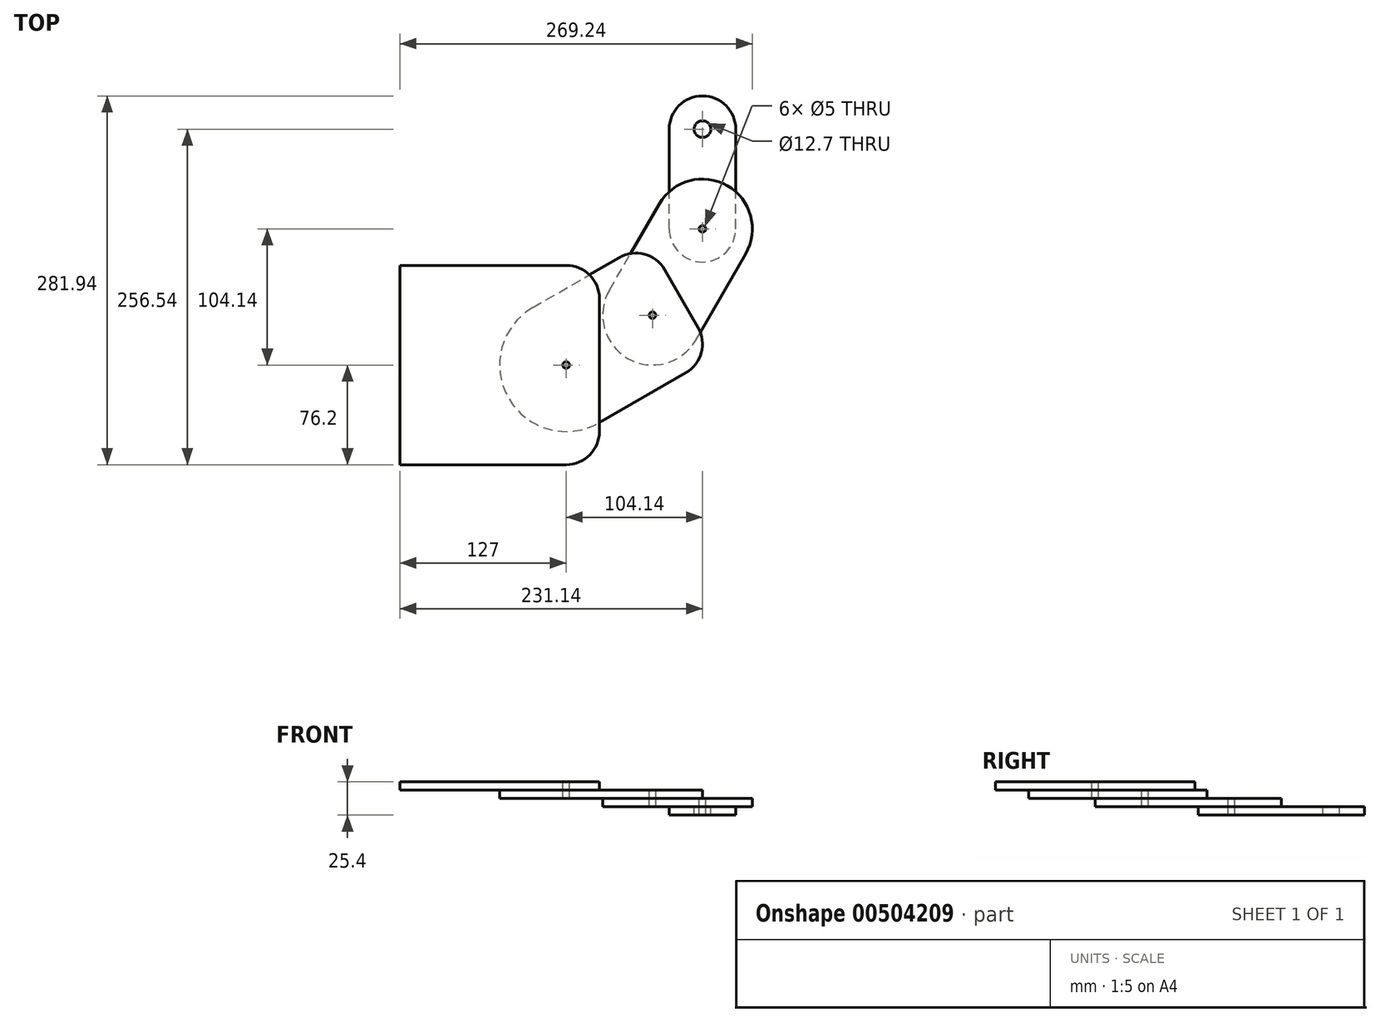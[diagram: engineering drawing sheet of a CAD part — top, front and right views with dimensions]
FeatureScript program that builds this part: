
annotation { "Feature Type Name" : "Feature", "Feature Type Description" : "" }
export const myFeature = defineFeature(function(context is Context, id is Id, definition is map)
    precondition{}
    {
        {
            var Q0;
            Q0=qCreatedBy(makeId("Top.planeOp"),FACE);
            var sketch = newSketch(context, id + "F0", { "sketchPlane" : qUnion([Q0])});
            skLineSegment(sketch, "E0.bottom", {"start": v(0, 76.2) * mm, "end": v(127, 76.2) * mm});
            skLineSegment(sketch, "E0.top", {"start": v(0, -76.2) * mm, "end": v(127, -76.2) * mm});
            skLineSegment(sketch, "E0.left", {"start": v(0, 76.2) * mm, "end": v(0, -76.2) * mm});
            skLineSegment(sketch, "E0.right", {"start": v(152.4, 50.8) * mm, "end": v(152.4, -50.8) * mm});
            skLineSegment(sketch, "E1", {"start": v(0, 0) * mm, "end": v(152.4, 0) * mm, "construction": true});
            skPoint(sketch, "E2.visualSharp", {"position": v(152.4, 76.2) * mm});
            skArc(sketch, "E2.filletArc", {"start": v(152.4, 50.8) * mm, "mid": v(144.96, 68.76) * mm, "end": v(127, 76.2) * mm});
            skPoint(sketch, "E3.visualSharp", {"position": v(152.4, -76.2) * mm});
            skArc(sketch, "E3.filletArc", {"start": v(127, -76.2) * mm, "mid": v(144.96, -68.76) * mm, "end": v(152.4, -50.8) * mm});
            skLineSegment(sketch, "E4", {"start": v(127, 50.8) * mm, "end": v(127, -50.8) * mm, "construction": true});
            skPoint(sketch, "E5", {"position": v(127, 0) * mm});
            skCircle(sketch, "E6", {"center": v(127, 0) * mm, "radius": 2.5 * mm});
            skSolve(sketch);
        }
        {
            var Q0;
            Q0=makeQuery(id+"F0.imprint","IMPRINT",FACE,{"disambiguationData":[TD([[makeQuery(id+"F0.imprint","IMPRINT",EDGE,{"derivedFrom":sQuery(id+"F0.wireOp",EDGE,"E0.bottom")}),-1.0]])]});
            extrude(context, id + "F1", {"entities" : qUnion([Q0]), "oppositeDirection" : true, "depth" : 6.35 * mm});
        }
        {
            var Q0;
            Q0=makeQuery(id+"F1.opExtrude","CAP_FACE",FACE,{"disambiguationData":[OSD([sQuery(id+"F0.wireOp",EDGE,"E0.bottom"),sQuery(id+"F0.wireOp",EDGE,"E0.top"),sQuery(id+"F0.wireOp",EDGE,"E0.left"),sQuery(id+"F0.wireOp",EDGE,"E0.right"),sQuery(id+"F0.wireOp",EDGE,"E2.filletArc"),sQuery(id+"F0.wireOp",EDGE,"E3.filletArc"),sQuery(id+"F0.wireOp",EDGE,"E6")])],"isStart":false});
            var sketch = newSketch(context, id + "F2", { "sketchPlane" : qUnion([Q0])});
            skLineSegment(sketch, "E7.bottom", {"start": v(127, 50.8) * mm, "end": v(203.2, 50.8) * mm});
            skLineSegment(sketch, "E7.top", {"start": v(127, -50.8) * mm, "end": v(203.2, -50.8) * mm});
            skLineSegment(sketch, "E7.left", {"start": v(76.2, 0) * mm, "end": v(76.2, 0) * mm});
            skLineSegment(sketch, "E7.right", {"start": v(228.6, 25.4) * mm, "end": v(228.6, -25.4) * mm});
            skPoint(sketch, "E8.visualSharp", {"position": v(76.2, 50.8) * mm});
            skArc(sketch, "E8.filletArc", {"start": v(127, 50.8) * mm, "mid": v(91.08, 35.92) * mm, "end": v(76.2, 0) * mm});
            skPoint(sketch, "E9.visualSharp", {"position": v(76.2, -50.8) * mm});
            skArc(sketch, "E9.filletArc", {"start": v(76.2, 0) * mm, "mid": v(91.08, -35.92) * mm, "end": v(127, -50.8) * mm});
            skPoint(sketch, "E10.visualSharp", {"position": v(228.6, 50.8) * mm});
            skArc(sketch, "E10.filletArc", {"start": v(228.6, 25.4) * mm, "mid": v(221.16, 43.36) * mm, "end": v(203.2, 50.8) * mm});
            skPoint(sketch, "E11.visualSharp", {"position": v(228.6, -50.8) * mm});
            skArc(sketch, "E11.filletArc", {"start": v(203.2, -50.8) * mm, "mid": v(221.16, -43.36) * mm, "end": v(228.6, -25.4) * mm});
            skLineSegment(sketch, "E12", {"start": v(203.2, 25.4) * mm, "end": v(203.2, -25.4) * mm, "construction": true});
            skLineSegment(sketch, "E13", {"start": v(127, 0) * mm, "end": v(203.2, 0) * mm, "construction": true});
            skCircle(sketch, "E14", {"center": v(127, 0) * mm, "radius": 2.5 * mm});
            skCircle(sketch, "E15", {"center": v(203.2, 0) * mm, "radius": 2.5 * mm});
            skSolve(sketch);
        }
        {
            var Q0;
            Q0=makeQuery(id+"F2.imprint","IMPRINT",FACE,{"disambiguationData":[TD([[makeQuery(id+"F2.imprint","IMPRINT",EDGE,{"derivedFrom":sQuery(id+"F2.wireOp",EDGE,"E7.bottom")}),-1.0]])]});
            var Q1;
            Q1=makeQuery(id+"F2.imprint","IMPRINT",FACE,{"disambiguationData":[TD([[makeQuery(id+"F2.imprint","IMPRINT",EDGE,{"derivedFrom":sQuery(id+"F2.wireOp",EDGE,"E7.right")}),-1.0]])]});
            extrude(context, id + "F3", {"entities" : qUnion([Q0, Q1]), "depth" : 6.35 * mm});
        }
        {
            var Q0;
            Q0=makeQuery(id+"F3.opExtrude","CAP_FACE",FACE,{"disambiguationData":[OSD([sQuery(id+"F2.wireOp",EDGE,"E7.bottom"),sQuery(id+"F2.wireOp",EDGE,"E7.top"),sQuery(id+"F2.wireOp",EDGE,"E7.right"),sQuery(id+"F2.wireOp",EDGE,"E8.filletArc"),sQuery(id+"F2.wireOp",EDGE,"E9.filletArc"),sQuery(id+"F2.wireOp",EDGE,"E10.filletArc"),sQuery(id+"F2.wireOp",EDGE,"E11.filletArc"),sQuery(id+"F2.wireOp",EDGE,"E14"),sQuery(id+"F2.wireOp",EDGE,"E15")])],"isStart":false});
            var sketch = newSketch(context, id + "F4", { "sketchPlane" : qUnion([Q0])});
            skLineSegment(sketch, "E16.bottom", {"start": v(203.2, 38.1) * mm, "end": v(279.4, 38.1) * mm});
            skLineSegment(sketch, "E16.top", {"start": v(203.2, -38.1) * mm, "end": v(279.4, -38.1) * mm});
            skLineSegment(sketch, "E16.left", {"start": v(165.1, 0) * mm, "end": v(165.1, 0) * mm});
            skLineSegment(sketch, "E16.right", {"start": v(317.5, 0) * mm, "end": v(317.5, 0) * mm});
            skPoint(sketch, "E17.visualSharp", {"position": v(165.1, 38.1) * mm});
            skArc(sketch, "E17.filletArc", {"start": v(203.2, 38.1) * mm, "mid": v(176.26, 26.94) * mm, "end": v(165.1, 0) * mm});
            skPoint(sketch, "E18.visualSharp", {"position": v(165.1, -38.1) * mm});
            skArc(sketch, "E18.filletArc", {"start": v(165.1, 0) * mm, "mid": v(176.26, -26.94) * mm, "end": v(203.2, -38.1) * mm});
            skCircle(sketch, "E19", {"center": v(203.2, 0) * mm, "radius": 2.5 * mm});
            skPoint(sketch, "E20.visualSharp", {"position": v(317.5, 38.1) * mm});
            skArc(sketch, "E20.filletArc", {"start": v(317.5, 0) * mm, "mid": v(306.34, 26.94) * mm, "end": v(279.4, 38.1) * mm});
            skPoint(sketch, "E21.visualSharp", {"position": v(317.5, -38.1) * mm});
            skArc(sketch, "E21.filletArc", {"start": v(279.4, -38.1) * mm, "mid": v(306.34, -26.94) * mm, "end": v(317.5, 0) * mm});
            skCircle(sketch, "E22", {"center": v(279.4, 0) * mm, "radius": 2.5 * mm});
            skSolve(sketch);
        }
        {
            var Q0;
            {var subQ0=sQuery(id+"F4.wireOp",EDGE,"E20.filletArc");Q0=makeQuery(id+"F4.imprint","IMPRINT",FACE,{"disambiguationData":[TD([[makeQuery(id+"F4.imprint","IMPRINT",EDGE,{"derivedFrom":subQ0}),1.0]])]});}
            var Q1;
            {var subQ0=sQuery(id+"F4.wireOp",EDGE,"E17.filletArc");Q1=makeQuery(id+"F4.imprint","IMPRINT",FACE,{"disambiguationData":[TD([[makeQuery(id+"F4.imprint","IMPRINT",EDGE,{"derivedFrom":subQ0}),1.0]])]});}
            extrude(context, id + "F5", {"entities" : qUnion([Q0, Q1]), "depth" : 6.35 * mm});
        }
        {
            var Q0;
            Q0=makeQuery(id+"F5.opExtrude","CAP_FACE",FACE,{"disambiguationData":[OSD([sQuery(id+"F4.wireOp",EDGE,"E16.bottom"),sQuery(id+"F4.wireOp",EDGE,"E16.top"),sQuery(id+"F4.wireOp",EDGE,"E17.filletArc"),sQuery(id+"F4.wireOp",EDGE,"E18.filletArc"),sQuery(id+"F4.wireOp",EDGE,"E19"),sQuery(id+"F4.wireOp",EDGE,"E20.filletArc"),sQuery(id+"F4.wireOp",EDGE,"E21.filletArc"),sQuery(id+"F4.wireOp",EDGE,"E22")])],"isStart":false});
            var sketch = newSketch(context, id + "F6", { "sketchPlane" : qUnion([Q0])});
            skLineSegment(sketch, "E23.bottom", {"start": v(279.4, 25.4) * mm, "end": v(355.6, 25.4) * mm});
            skLineSegment(sketch, "E23.top", {"start": v(279.4, -25.4) * mm, "end": v(355.6, -25.4) * mm});
            skLineSegment(sketch, "E23.left", {"start": v(254, 0) * mm, "end": v(254, 0) * mm});
            skLineSegment(sketch, "E23.right", {"start": v(381, 0) * mm, "end": v(381, 0) * mm});
            skPoint(sketch, "E24.visualSharp", {"position": v(254, 25.4) * mm});
            skArc(sketch, "E24.filletArc", {"start": v(279.4, 25.4) * mm, "mid": v(261.44, 17.96) * mm, "end": v(254, 0) * mm});
            skPoint(sketch, "E25.visualSharp", {"position": v(254, -25.4) * mm});
            skArc(sketch, "E25.filletArc", {"start": v(254, 0) * mm, "mid": v(261.44, -17.96) * mm, "end": v(279.4, -25.4) * mm});
            skPoint(sketch, "E26.visualSharp", {"position": v(381, -25.4) * mm});
            skArc(sketch, "E26.filletArc", {"start": v(355.6, -25.4) * mm, "mid": v(373.56, -17.96) * mm, "end": v(381, 0) * mm});
            skPoint(sketch, "E27.visualSharp", {"position": v(381, 25.4) * mm});
            skArc(sketch, "E27.filletArc", {"start": v(381, 0) * mm, "mid": v(373.56, 17.96) * mm, "end": v(355.6, 25.4) * mm});
            skCircle(sketch, "E28", {"center": v(279.4, 0) * mm, "radius": 2.5 * mm});
            skCircle(sketch, "E29", {"center": v(355.6, 0) * mm, "radius": 6.35 * mm});
            skSolve(sketch);
        }
        {
            var Q0;
            {var subQ0=sQuery(id+"F6.wireOp",EDGE,"E24.filletArc");Q0=makeQuery(id+"F6.imprint","IMPRINT",FACE,{"disambiguationData":[TD([[makeQuery(id+"F6.imprint","IMPRINT",EDGE,{"derivedFrom":subQ0}),1.0]])]});}
            var Q1;
            {var subQ1=sQuery(id+"F6.wireOp",EDGE,"E26.filletArc");Q1=makeQuery(id+"F6.imprint","IMPRINT",FACE,{"disambiguationData":[TD([[makeQuery(id+"F6.imprint","IMPRINT",EDGE,{"derivedFrom":subQ1}),1.0]])]});}
            extrude(context, id + "F7", {"entities" : qUnion([Q0, Q1]), "depth" : 6.35 * mm});
        }
        {
            var Q0;
            Q0=makeQuery(id+"F3.opExtrude","SWEPT_BODY",BODY,{"disambiguationData":[OSD([sQuery(id+"F2.wireOp",EDGE,"E7.bottom"),sQuery(id+"F2.wireOp",EDGE,"E7.top"),sQuery(id+"F2.wireOp",EDGE,"E7.right"),sQuery(id+"F2.wireOp",EDGE,"E8.filletArc"),sQuery(id+"F2.wireOp",EDGE,"E9.filletArc"),sQuery(id+"F2.wireOp",EDGE,"E10.filletArc"),sQuery(id+"F2.wireOp",EDGE,"E11.filletArc"),sQuery(id+"F2.wireOp",EDGE,"E14"),sQuery(id+"F2.wireOp",EDGE,"E15")])]});
            var Q1;
            Q1=makeQuery(id+"F1.opExtrude","CAP_EDGE",EDGE,{"disambiguationData":[OSD([sQuery(id+"F0.wireOp",EDGE,"E6")])],"isStart":true});
            transform(context, id + "F8", {"entities" : qUnion([Q0]), "transformType" : TransformType.ROTATION, "transformAxis" : qUnion([Q1]), "angle" : 30 * degree, "makeCopy" : false});
        }
        {
            var Q0;
            Q0=makeQuery(id+"F5.opExtrude","SWEPT_BODY",BODY,{"disambiguationData":[OSD([sQuery(id+"F4.wireOp",EDGE,"E16.bottom"),sQuery(id+"F4.wireOp",EDGE,"E16.top"),sQuery(id+"F4.wireOp",EDGE,"E17.filletArc"),sQuery(id+"F4.wireOp",EDGE,"E18.filletArc"),sQuery(id+"F4.wireOp",EDGE,"E19"),sQuery(id+"F4.wireOp",EDGE,"E20.filletArc"),sQuery(id+"F4.wireOp",EDGE,"E21.filletArc"),sQuery(id+"F4.wireOp",EDGE,"E22")])]});
            transform(context, id + "F9", {"entities" : qUnion([Q0]), "transformType" : TransformType.TRANSLATION_3D, "dx" : -10.16 * mm, "dy" : 38.1 * mm, "dz" : 0 * mm, "makeCopy" : false});
        }
        {
            var Q0;
            Q0=makeQuery(id+"F5.opExtrude","SWEPT_BODY",BODY,{"disambiguationData":[OSD([sQuery(id+"F4.wireOp",EDGE,"E16.bottom"),sQuery(id+"F4.wireOp",EDGE,"E16.top"),sQuery(id+"F4.wireOp",EDGE,"E17.filletArc"),sQuery(id+"F4.wireOp",EDGE,"E18.filletArc"),sQuery(id+"F4.wireOp",EDGE,"E19"),sQuery(id+"F4.wireOp",EDGE,"E20.filletArc"),sQuery(id+"F4.wireOp",EDGE,"E21.filletArc"),sQuery(id+"F4.wireOp",EDGE,"E22")])]});
            var Q1;
            Q1=makeQuery(id+"F5.opExtrude","CAP_EDGE",EDGE,{"disambiguationData":[OSD([sQuery(id+"F4.wireOp",EDGE,"E19")])],"isStart":false});
            transform(context, id + "F10", {"entities" : qUnion([Q0]), "transformType" : TransformType.ROTATION, "transformAxis" : qUnion([Q1]), "angle" : 60 * degree, "oppositeDirection" : true, "makeCopy" : false});
        }
        {
            var Q0;
            Q0=makeQuery(id+"F7.opExtrude","SWEPT_BODY",BODY,{"disambiguationData":[OSD([sQuery(id+"F6.wireOp",EDGE,"E23.bottom"),sQuery(id+"F6.wireOp",EDGE,"E23.top"),sQuery(id+"F6.wireOp",EDGE,"E24.filletArc"),sQuery(id+"F6.wireOp",EDGE,"E25.filletArc"),sQuery(id+"F6.wireOp",EDGE,"E26.filletArc"),sQuery(id+"F6.wireOp",EDGE,"E27.filletArc"),sQuery(id+"F6.wireOp",EDGE,"E28"),sQuery(id+"F6.wireOp",EDGE,"E29")])]});
            transform(context, id + "F11", {"entities" : qUnion([Q0]), "transformType" : TransformType.TRANSLATION_3D, "dx" : -48.26 * mm, "dy" : 104.14 * mm, "dz" : 0 * mm, "makeCopy" : false});
        }
        {
            var Q0;
            Q0=makeQuery(id+"F7.opExtrude","SWEPT_BODY",BODY,{"disambiguationData":[OSD([sQuery(id+"F6.wireOp",EDGE,"E23.bottom"),sQuery(id+"F6.wireOp",EDGE,"E23.top"),sQuery(id+"F6.wireOp",EDGE,"E24.filletArc"),sQuery(id+"F6.wireOp",EDGE,"E25.filletArc"),sQuery(id+"F6.wireOp",EDGE,"E26.filletArc"),sQuery(id+"F6.wireOp",EDGE,"E27.filletArc"),sQuery(id+"F6.wireOp",EDGE,"E28"),sQuery(id+"F6.wireOp",EDGE,"E29")])]});
            var Q1;
            Q1=makeQuery(id+"F7.opExtrude","CAP_EDGE",EDGE,{"disambiguationData":[OSD([sQuery(id+"F6.wireOp",EDGE,"E28")])],"isStart":false});
            transform(context, id + "F12", {"entities" : qUnion([Q0]), "transformType" : TransformType.ROTATION, "transformAxis" : qUnion([Q1]), "angle" : 90 * degree, "oppositeDirection" : true, "makeCopy" : false});
        }
    });
